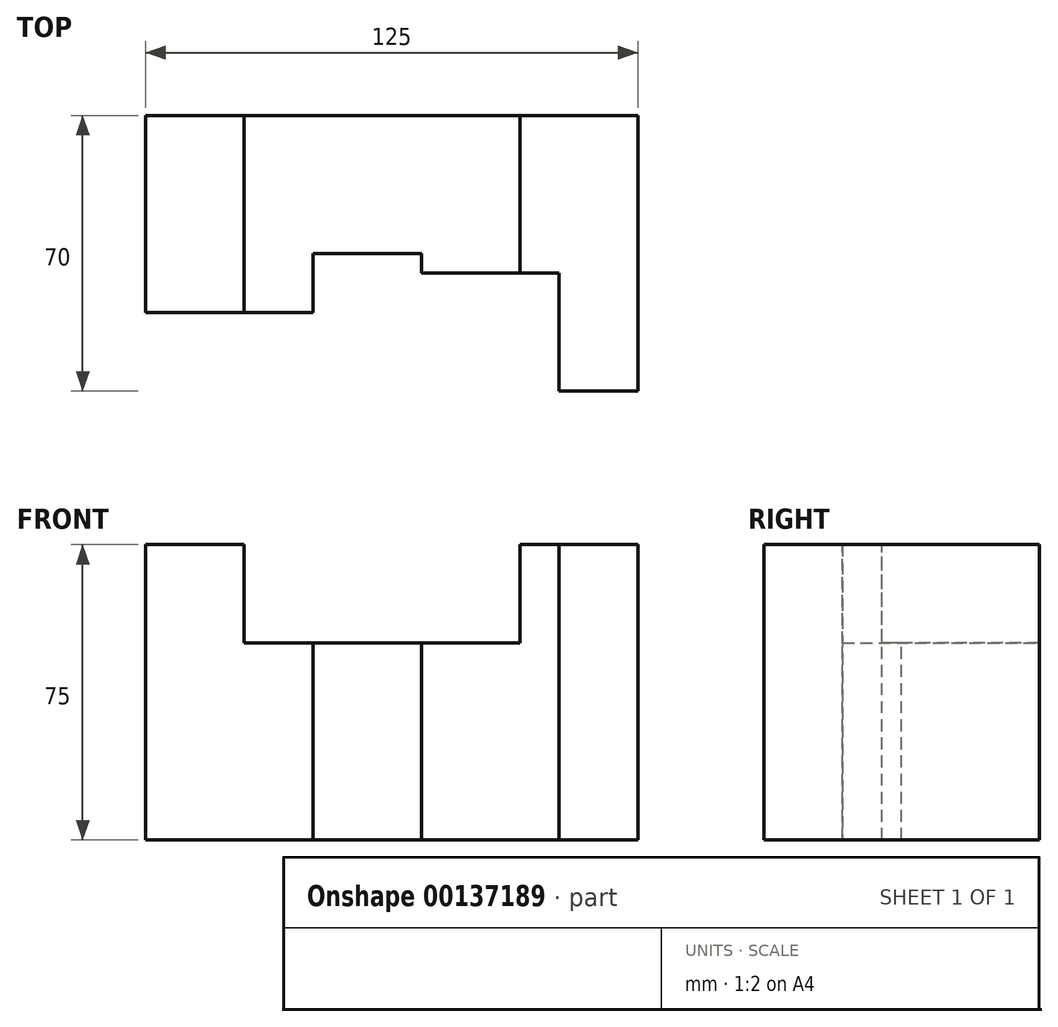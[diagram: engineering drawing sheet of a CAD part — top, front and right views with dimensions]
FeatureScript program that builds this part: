
annotation { "Feature Type Name" : "Feature", "Feature Type Description" : "" }
export const myFeature = defineFeature(function(context is Context, id is Id, definition is map)
    precondition{}
    {
        {
            var Q0;
            Q0=qCreatedBy(makeId("Front.planeOp"),FACE);
            var sketch = newSketch(context, id + "F0", { "sketchPlane" : qUnion([Q0])});
            skLineSegment(sketch, "E0", {"start": v(0, 0) * mm, "end": v(25, 0) * mm});
            skLineSegment(sketch, "E1", {"start": v(25, 0) * mm, "end": v(25, 75) * mm});
            skLineSegment(sketch, "E2", {"start": v(25, 75) * mm, "end": v(0, 75) * mm});
            skLineSegment(sketch, "E3", {"start": v(0, 75) * mm, "end": v(0, 0) * mm});
            skLineSegment(sketch, "E4", {"start": v(25, 0) * mm, "end": v(42.5, 0) * mm});
            skLineSegment(sketch, "E5", {"start": v(42.5, 0) * mm, "end": v(42.5, 50) * mm});
            skLineSegment(sketch, "E6", {"start": v(42.5, 50) * mm, "end": v(25, 50) * mm});
            skSolve(sketch);
        }
        {
            var Q0;
            Q0 = qSketchRegion(id + "F0", true);
            extrude(context, id + "F1", {"entities" : qUnion([Q0]), "endBound" : BoundingType.SYMMETRIC, "depth" : 50 * mm});
        }
        {
            var Q0;
            Q0=makeQuery(id+"F1.opExtrude","SWEPT_FACE",FACE,{"disambiguationData":[OSD([sQuery(id+"F0.wireOp",EDGE,"E5")])]});
            var sketch = newSketch(context, id + "F2", { "sketchPlane" : qUnion([Q0])});
            skLineSegment(sketch, "E7.bottom", {"start": v(25, 0) * mm, "end": v(-10, 0) * mm});
            skLineSegment(sketch, "E7.top", {"start": v(25, 50) * mm, "end": v(-10, 50) * mm});
            skLineSegment(sketch, "E7.left", {"start": v(25, 0) * mm, "end": v(25, 50) * mm});
            skLineSegment(sketch, "E7.right", {"start": v(-10, 0) * mm, "end": v(-10, 50) * mm});
            skSolve(sketch);
        }
        {
            var Q0;
            Q0 = qSketchRegion(id + "F2", true);
            extrude(context, id + "F3", {"entities" : qUnion([Q0]), "operationType" : NewBodyOperationType.ADD, "depth" : 5.5 * 5 * mm});
        }
        {
            var Q0;
            Q0=makeQuery(id+"F3.opExtrude","CAP_FACE",FACE,{"disambiguationData":[OSD([sQuery(id+"F2.wireOp",EDGE,"E7.bottom"),sQuery(id+"F2.wireOp",EDGE,"E7.top"),sQuery(id+"F2.wireOp",EDGE,"E7.left"),sQuery(id+"F2.wireOp",EDGE,"E7.right")])],"isStart":false});
            var sketch = newSketch(context, id + "F4", { "sketchPlane" : qUnion([Q0])});
            skLineSegment(sketch, "E8.bottom", {"start": v(25, 0) * mm, "end": v(-15, 0) * mm});
            skLineSegment(sketch, "E8.top", {"start": v(25, 50) * mm, "end": v(-15, 50) * mm});
            skLineSegment(sketch, "E8.left", {"start": v(25, 0) * mm, "end": v(25, 50) * mm});
            skLineSegment(sketch, "E8.right", {"start": v(-15, 0) * mm, "end": v(-15, 50) * mm});
            skSolve(sketch);
        }
        {
            var Q0;
            Q0 = qSketchRegion(id + "F4", true);
            extrude(context, id + "F5", {"entities" : qUnion([Q0]), "operationType" : NewBodyOperationType.ADD, "depth" : 25 * mm});
        }
        {
            var Q0;
            Q0=makeQuery(id+"F5.opExtrude","CAP_FACE",FACE,{"disambiguationData":[OSD([sQuery(id+"F4.wireOp",EDGE,"E8.bottom"),sQuery(id+"F4.wireOp",EDGE,"E8.top"),sQuery(id+"F4.wireOp",EDGE,"E8.left"),sQuery(id+"F4.wireOp",EDGE,"E8.right")])],"isStart":false});
            var sketch = newSketch(context, id + "F6", { "sketchPlane" : qUnion([Q0])});
            skLineSegment(sketch, "E9.bottom", {"start": v(25, 0) * mm, "end": v(-15, 0) * mm});
            skLineSegment(sketch, "E9.top", {"start": v(25, 75) * mm, "end": v(-15, 75) * mm});
            skLineSegment(sketch, "E9.left", {"start": v(25, 0) * mm, "end": v(25, 75) * mm});
            skLineSegment(sketch, "E9.right", {"start": v(-15, 0) * mm, "end": v(-15, 75) * mm});
            skSolve(sketch);
        }
        {
            var Q0;
            Q0 = qSketchRegion(id + "F6", true);
            extrude(context, id + "F7", {"entities" : qUnion([Q0]), "operationType" : NewBodyOperationType.ADD, "depth" : 30 * mm});
        }
        {
            var Q0;
            Q0=makeQuery(id+"F7.boolean.opBoolean","MERGE",FACE,{"derivedFrom":[makeQuery(id+"F5.opExtrude","SWEPT_FACE",FACE,{"disambiguationData":[OSD([sQuery(id+"F4.wireOp",EDGE,"E8.right")])]}),makeQuery(id+"F7.opExtrude","SWEPT_FACE",FACE,{"disambiguationData":[OSD([sQuery(id+"F6.wireOp",EDGE,"E9.right")])]})]});
            var sketch = newSketch(context, id + "F8", { "sketchPlane" : qUnion([Q0])});
            skLineSegment(sketch, "E10.bottom", {"start": v(125, 0) * mm, "end": v(105, 0) * mm});
            skLineSegment(sketch, "E10.top", {"start": v(125, 75) * mm, "end": v(105, 75) * mm});
            skLineSegment(sketch, "E10.left", {"start": v(125, 0) * mm, "end": v(125, 75) * mm});
            skLineSegment(sketch, "E10.right", {"start": v(105, 0) * mm, "end": v(105, 75) * mm});
            skSolve(sketch);
        }
        {
            var Q0;
            Q0 = qSketchRegion(id + "F8", true);
            extrude(context, id + "F9", {"entities" : qUnion([Q0]), "operationType" : NewBodyOperationType.ADD, "depth" : 30 * mm});
        }
    });
